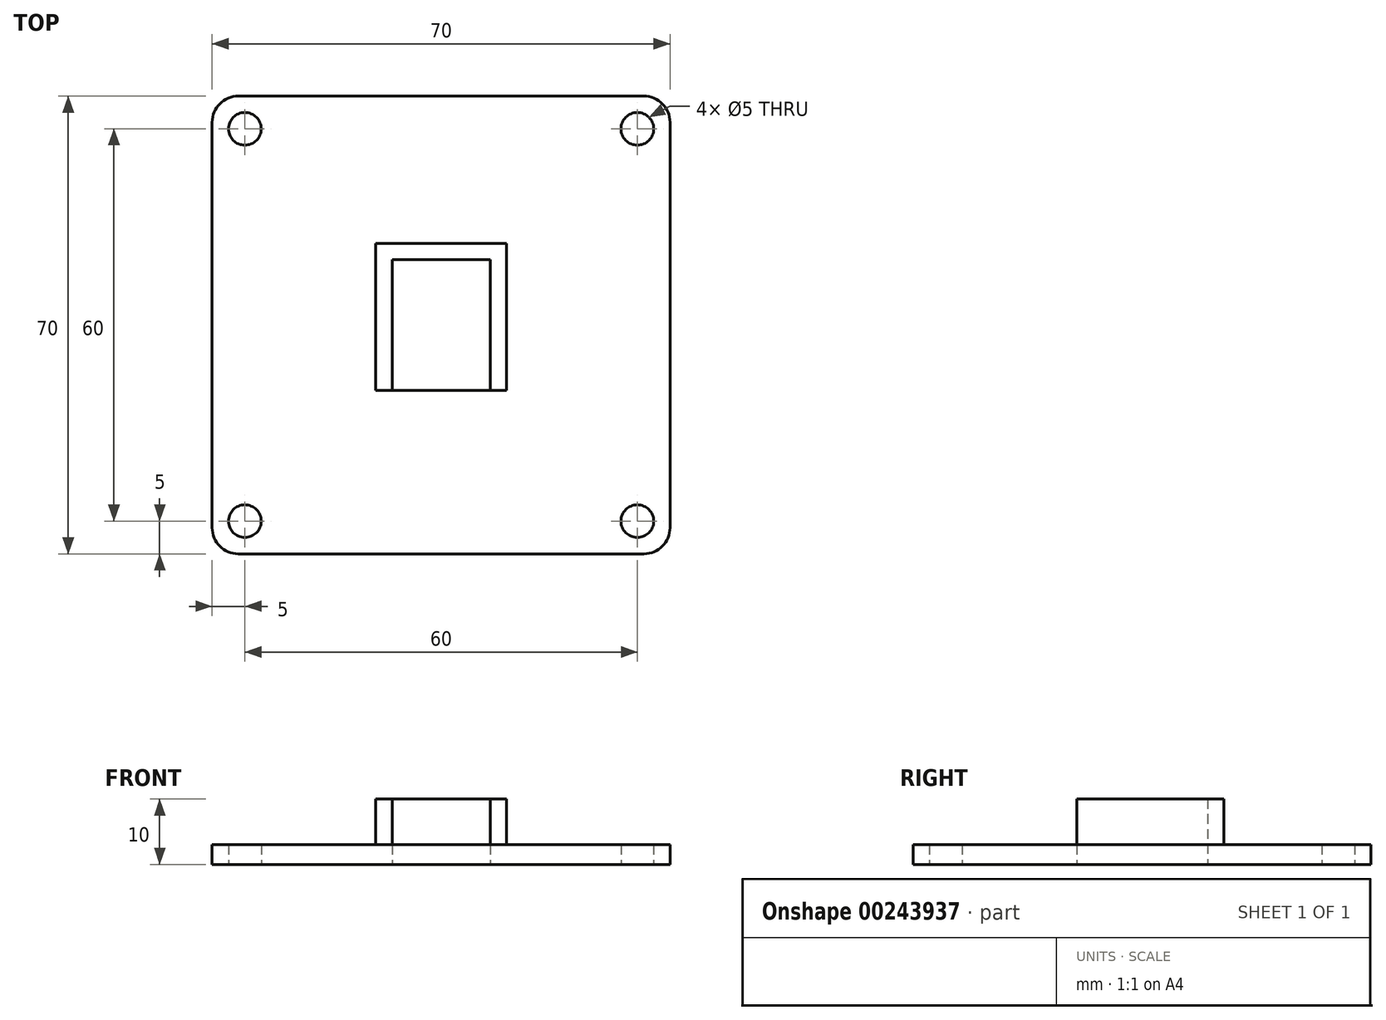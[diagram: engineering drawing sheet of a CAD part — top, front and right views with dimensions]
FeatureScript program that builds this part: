
annotation { "Feature Type Name" : "Feature", "Feature Type Description" : "" }
export const myFeature = defineFeature(function(context is Context, id is Id, definition is map)
    precondition{}
    {
        {
            var Q0;
            Q0=qCreatedBy(makeId("Top.planeOp"),FACE);
            var sketch = newSketch(context, id + "F0", { "sketchPlane" : qUnion([Q0])});
            skLineSegment(sketch, "E0.bottom", {"start": v(4, 0) * mm, "end": v(66, 0) * mm});
            skLineSegment(sketch, "E0.top", {"start": v(4, 70) * mm, "end": v(66, 70) * mm});
            skLineSegment(sketch, "E0.left", {"start": v(0, 4) * mm, "end": v(0, 66) * mm});
            skLineSegment(sketch, "E0.right", {"start": v(70, 4) * mm, "end": v(70, 66) * mm});
            skLineSegment(sketch, "E1.0", {"start": v(5, 5) * mm, "end": v(5, 65) * mm, "construction": true});
            skLineSegment(sketch, "E2.0", {"start": v(5, 5) * mm, "end": v(65, 5) * mm, "construction": true});
            skLineSegment(sketch, "E3.0", {"start": v(65, 5) * mm, "end": v(65, 65) * mm, "construction": true});
            skLineSegment(sketch, "E4.0", {"start": v(5, 65) * mm, "end": v(65, 65) * mm, "construction": true});
            skCircle(sketch, "E5", {"center": v(5, 65) * mm, "radius": 2.5 * mm});
            skCircle(sketch, "E6", {"center": v(65, 65) * mm, "radius": 2.5 * mm});
            skCircle(sketch, "E7", {"center": v(5, 5) * mm, "radius": 2.5 * mm});
            skCircle(sketch, "E8", {"center": v(65, 5) * mm, "radius": 2.5 * mm});
            skLineSegment(sketch, "E9.0", {"start": v(42.5, 25) * mm, "end": v(42.5, 45) * mm});
            skLineSegment(sketch, "E10.0", {"start": v(27.5, 25) * mm, "end": v(27.5, 45) * mm});
            skLineSegment(sketch, "E11.0", {"start": v(25, 25) * mm, "end": v(45, 25) * mm});
            skLineSegment(sketch, "E12.0", {"start": v(27.5, 45) * mm, "end": v(42.5, 45) * mm});
            skLineSegment(sketch, "E13.0", {"start": v(25, 25) * mm, "end": v(25, 47.5) * mm});
            skLineSegment(sketch, "E14.0", {"start": v(25, 47.5) * mm, "end": v(45, 47.5) * mm});
            skLineSegment(sketch, "E15.0", {"start": v(45, 25) * mm, "end": v(45, 47.5) * mm});
            skPoint(sketch, "E16.visualSharp", {"position": v(0, 70) * mm});
            skArc(sketch, "E16.filletArc", {"start": v(4, 70) * mm, "mid": v(1.17, 68.83) * mm, "end": v(0, 66) * mm});
            skPoint(sketch, "E17.visualSharp", {"position": v(70, 70) * mm});
            skArc(sketch, "E17.filletArc", {"start": v(70, 66) * mm, "mid": v(68.83, 68.83) * mm, "end": v(66, 70) * mm});
            skPoint(sketch, "E18.visualSharp", {"position": v(70, 0) * mm});
            skArc(sketch, "E18.filletArc", {"start": v(66, 0) * mm, "mid": v(68.83, 1.17) * mm, "end": v(70, 4) * mm});
            skPoint(sketch, "E19.visualSharp", {"position": v(0, 0) * mm});
            skArc(sketch, "E19.filletArc", {"start": v(0, 4) * mm, "mid": v(1.17, 1.17) * mm, "end": v(4, 0) * mm});
            skSolve(sketch);
        }
        {
            var Q0;
            Q0=makeQuery(id+"F0.imprint","IMPRINT",FACE,{"disambiguationData":[TD([[makeQuery(id+"F0.imprint","IMPRINT",EDGE,{"derivedFrom":sQuery(id+"F0.wireOp",EDGE,"E0.bottom")}),1.0]])]});
            extrude(context, id + "F1", {"entities" : qUnion([Q0]), "depth" : 3 * mm, "offsetDistance" : 25 * mm});
        }
        {
            var Q0;
            {var subQ1=sQuery(id+"F0.wireOp",EDGE,"E9.0");Q0=makeQuery(id+"F0.imprint","IMPRINT",FACE,{"disambiguationData":[TD([[makeQuery(id+"F0.imprint","IMPRINT",EDGE,{"derivedFrom":subQ1}),-1.0]])]});}
            extrude(context, id + "F2", {"entities" : qUnion([Q0]), "operationType" : NewBodyOperationType.ADD, "depth" : 10 * mm, "offsetDistance" : 25 * mm});
        }
    });
